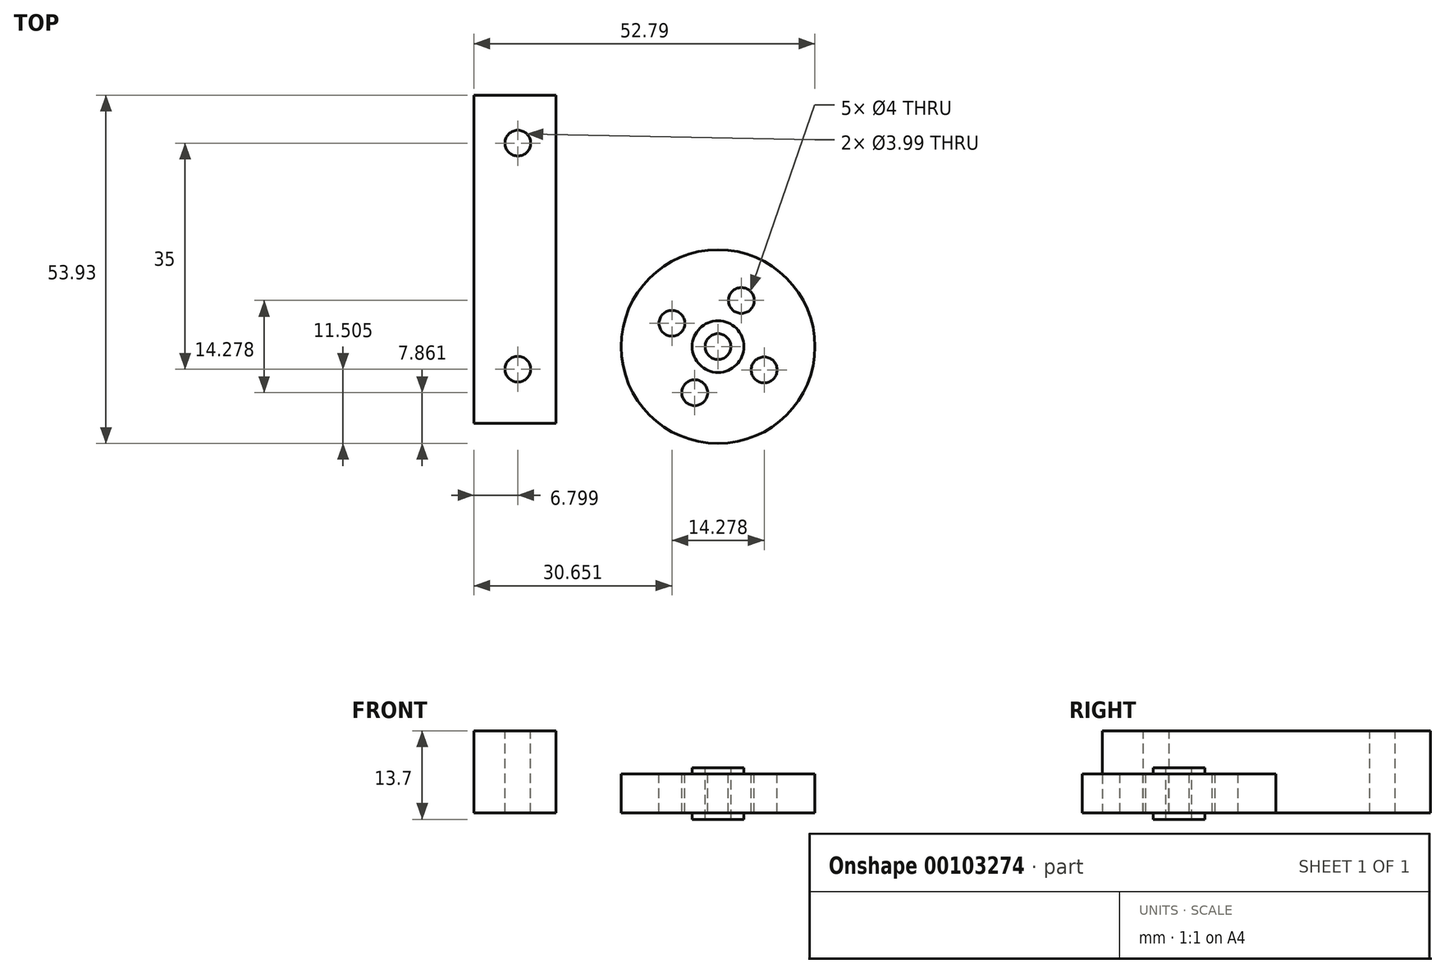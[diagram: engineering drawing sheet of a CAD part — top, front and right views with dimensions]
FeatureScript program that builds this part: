
annotation { "Feature Type Name" : "Feature", "Feature Type Description" : "" }
export const myFeature = defineFeature(function(context is Context, id is Id, definition is map)
    precondition{}
    {
        {
            var Q0;
            Q0=qCreatedBy(makeId("Top.planeOp"),FACE);
            var sketch = newSketch(context, id + "F0", { "sketchPlane" : qUnion([Q0])});
            skCircle(sketch, "E0", {"center": v(0, 0) * mm, "radius": 15 * mm});
            skSolve(sketch);
        }
        {
            var Q0;
            Q0=makeQuery(id+"F0.imprint","IMPRINT",FACE,{"disambiguationData":[TD([[makeQuery(id+"F0.imprint","IMPRINT",EDGE,{"derivedFrom":sQuery(id+"F0.wireOp",EDGE,"E0")}),1.0]])]});
            var Q1;
            Q1=sQuery(id+"F0.wireOp",EDGE,"E0");
            extrude(context, id + "F1", {"entities" : qUnion([Q0]), "surfaceEntities" : qUnion([Q1]), "depth" : 6 * mm});
        }
        {
            var Q0;
            Q0=makeQuery(id+"F1.opExtrude","CAP_FACE",FACE,{"disambiguationData":[OSD([sQuery(id+"F0.wireOp",EDGE,"E0")])],"isStart":false});
            var sketch = newSketch(context, id + "F2", { "sketchPlane" : qUnion([Q0])});
            skCircle(sketch, "E1", {"center": v(0, 0) * mm, "radius": 4 * mm});
            skCircle(sketch, "E2", {"center": v(0, 0) * mm, "radius": 2 * mm});
            skCircle(sketch, "E3", {"center": v(-7.14, 3.61) * mm, "radius": 2 * mm});
            skCircle(sketch, "E4.1.0", {"center": v(-3.61, -7.14) * mm, "radius": 2 * mm});
            skCircle(sketch, "E4.2.0", {"center": v(7.14, -3.61) * mm, "radius": 2 * mm});
            skCircle(sketch, "E4.3.0", {"center": v(3.61, 7.14) * mm, "radius": 2 * mm});
            skSolve(sketch);
        }
        {
            var Q0;
            Q0=makeQuery(id+"F2.imprint","IMPRINT",FACE,{"disambiguationData":[TD([[makeQuery(id+"F2.imprint","IMPRINT",EDGE,{"derivedFrom":sQuery(id+"F2.wireOp",EDGE,"E3")}),1.0]])]});
            var Q1;
            Q1=makeQuery(id+"F2.imprint","IMPRINT",FACE,{"disambiguationData":[TD([[makeQuery(id+"F2.imprint","IMPRINT",EDGE,{"derivedFrom":sQuery(id+"F2.wireOp",EDGE,"E4.3.0")}),1.0]])]});
            var Q2;
            Q2=makeQuery(id+"F2.imprint","IMPRINT",FACE,{"disambiguationData":[TD([[makeQuery(id+"F2.imprint","IMPRINT",EDGE,{"derivedFrom":sQuery(id+"F2.wireOp",EDGE,"E4.2.0")}),1.0]])]});
            var Q3;
            Q3=makeQuery(id+"F2.imprint","IMPRINT",FACE,{"disambiguationData":[TD([[makeQuery(id+"F2.imprint","IMPRINT",EDGE,{"derivedFrom":sQuery(id+"F2.wireOp",EDGE,"E4.1.0")}),1.0]])]});
            var Q4;
            Q4=makeQuery(id+"F2.imprint","IMPRINT",FACE,{"disambiguationData":[TD([[makeQuery(id+"F2.imprint","IMPRINT",EDGE,{"derivedFrom":sQuery(id+"F2.wireOp",EDGE,"E2")}),1.0]])]});
            extrude(context, id + "F3", {"entities" : qUnion([Q0, Q1, Q2, Q3, Q4]), "operationType" : NewBodyOperationType.REMOVE, "endBound" : BoundingType.THROUGH_ALL, "oppositeDirection" : true, "depth" : 25.4 * mm});
        }
        {
            var Q0;
            Q0=makeQuery(id+"F2.imprint","IMPRINT",FACE,{"disambiguationData":[TD([[makeQuery(id+"F2.imprint","IMPRINT",EDGE,{"derivedFrom":sQuery(id+"F2.wireOp",EDGE,"E1")}),1.0]])]});
            extrude(context, id + "F4", {"entities" : qUnion([Q0]), "operationType" : NewBodyOperationType.ADD, "depth" : 1 * mm});
        }
        {
            var Q0;
            Q0=makeQuery(id+"F1.opExtrude","CAP_FACE",FACE,{"disambiguationData":[OSD([sQuery(id+"F0.wireOp",EDGE,"E0")])],"isStart":true});
            var sketch = newSketch(context, id + "F5", { "sketchPlane" : qUnion([Q0])});
            skCircle(sketch, "E5", {"center": v(0, 0) * mm, "radius": 4 * mm});
            skSolve(sketch);
        }
        {
            var Q0;
            Q0=makeQuery(id+"F5.imprint","IMPRINT",FACE,{"disambiguationData":[TD([[makeQuery(id+"F5.imprint","IMPRINT",EDGE,{"derivedFrom":sQuery(id+"F5.wireOp",EDGE,"E5")}),1.0]])]});
            extrude(context, id + "F6", {"entities" : qUnion([Q0]), "operationType" : NewBodyOperationType.ADD, "depth" : 1 * mm});
        }
        {
            var Q0;
            Q0=qCreatedBy(makeId("Top.planeOp"),FACE);
            var sketch = newSketch(context, id + "F7", { "sketchPlane" : qUnion([Q0])});
            skLineSegment(sketch, "E6.bottom", {"start": v(-37.8, 38.93) * mm, "end": v(-25.1, 38.93) * mm});
            skLineSegment(sketch, "E6.top", {"start": v(-37.8, -11.87) * mm, "end": v(-25.1, -11.87) * mm});
            skLineSegment(sketch, "E6.left", {"start": v(-37.8, 38.93) * mm, "end": v(-37.8, -11.87) * mm});
            skLineSegment(sketch, "E6.right", {"start": v(-25.1, 38.93) * mm, "end": v(-25.1, -11.87) * mm});
            skSolve(sketch);
        }
        {
            var Q0;
            Q0=makeQuery(id+"F7.imprint","IMPRINT",FACE,{"disambiguationData":[TD([[makeQuery(id+"F7.imprint","IMPRINT",EDGE,{"derivedFrom":sQuery(id+"F7.wireOp",EDGE,"E6.bottom")}),-1.0]])]});
            extrude(context, id + "F8", {"entities" : qUnion([Q0]), "depth" : 12.7 * mm});
        }
        {
            var Q0;
            Q0=makeQuery(id+"F8.opExtrude","CAP_FACE",FACE,{"disambiguationData":[OSD([sQuery(id+"F7.wireOp",EDGE,"E6.bottom"),sQuery(id+"F7.wireOp",EDGE,"E6.top"),sQuery(id+"F7.wireOp",EDGE,"E6.left"),sQuery(id+"F7.wireOp",EDGE,"E6.right")])],"isStart":false});
            var sketch = newSketch(context, id + "F9", { "sketchPlane" : qUnion([Q0])});
            skCircle(sketch, "E7", {"center": v(-31, 31.5) * mm, "radius": 2 * mm});
            skCircle(sketch, "E8", {"center": v(-31, -3.5) * mm, "radius": 2 * mm});
            skSolve(sketch);
        }
        {
            var Q0;
            Q0=makeQuery(id+"F9.imprint","IMPRINT",FACE,{"disambiguationData":[TD([[makeQuery(id+"F9.imprint","IMPRINT",EDGE,{"derivedFrom":sQuery(id+"F9.wireOp",EDGE,"E7")}),1.0]])]});
            var Q1;
            Q1=makeQuery(id+"F9.imprint","IMPRINT",FACE,{"disambiguationData":[TD([[makeQuery(id+"F9.imprint","IMPRINT",EDGE,{"derivedFrom":sQuery(id+"F9.wireOp",EDGE,"E8")}),1.0]])]});
            extrude(context, id + "F10", {"entities" : qUnion([Q0, Q1]), "operationType" : NewBodyOperationType.REMOVE, "oppositeDirection" : true, "depth" : 25.4 * mm});
        }
    });
